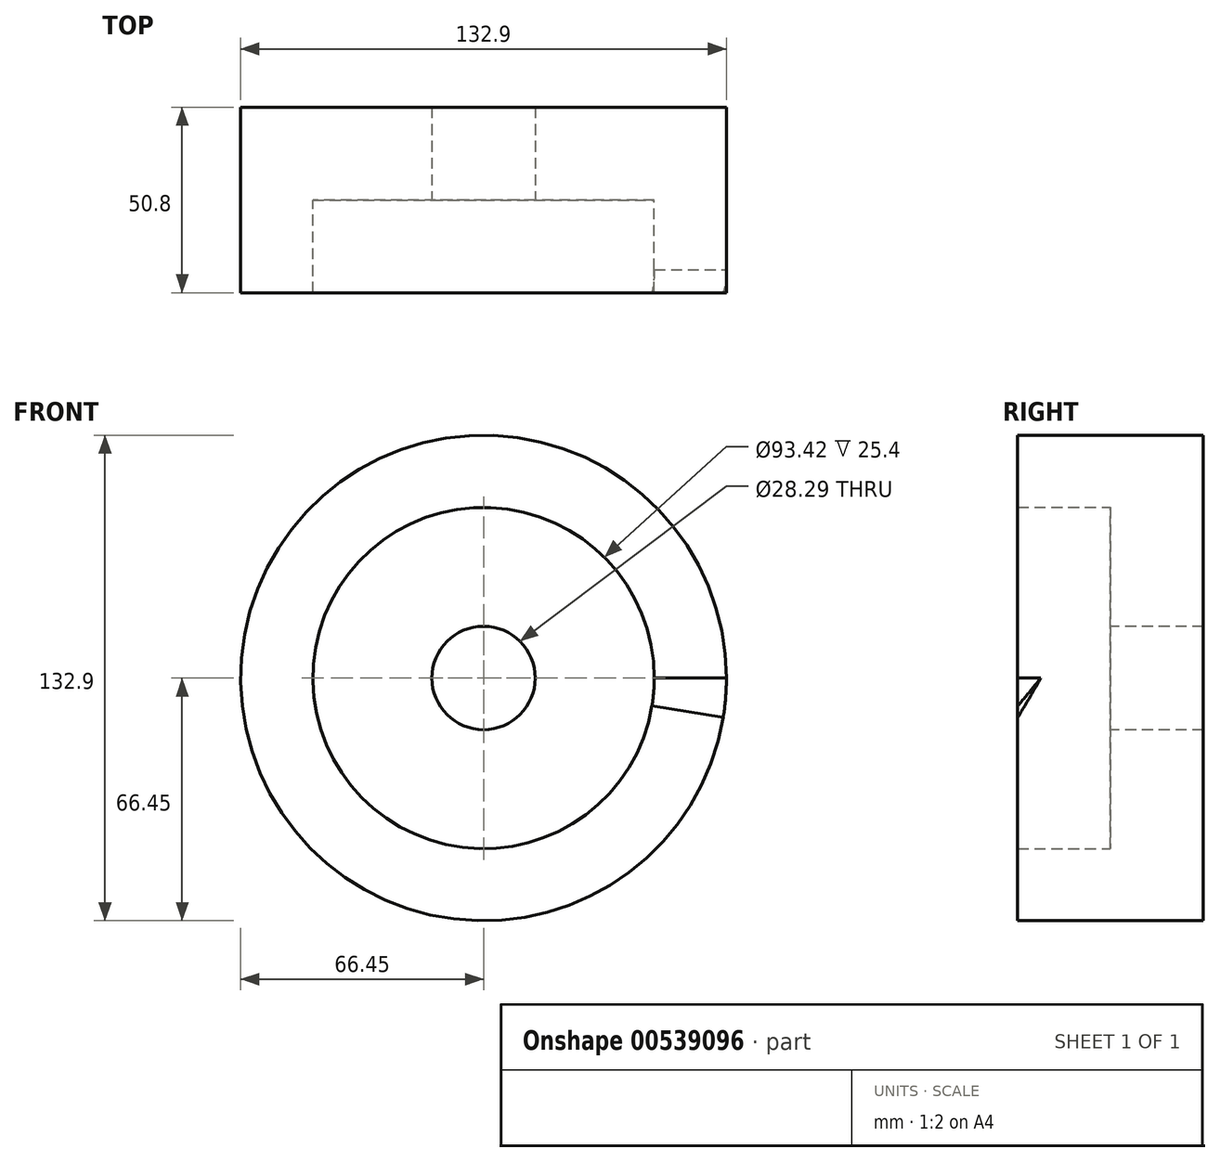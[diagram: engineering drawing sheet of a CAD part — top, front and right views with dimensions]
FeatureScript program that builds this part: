
annotation { "Feature Type Name" : "Feature", "Feature Type Description" : "" }
export const myFeature = defineFeature(function(context is Context, id is Id, definition is map)
    precondition{}
    {
        {
            var Q0;
            Q0=qCreatedBy(makeId("Front.planeOp"),FACE);
            var sketch = newSketch(context, id + "F0", { "sketchPlane" : qUnion([Q0])});
            skCircle(sketch, "E0", {"center": v(0, 0) * mm, "radius": 66.45 * mm});
            skSolve(sketch);
        }
        {
            var Q0;
            Q0 = qSketchRegion(id + "F0", true);
            extrude(context, id + "F1", {"entities" : qUnion([Q0]), "depth" : 25.4 * mm, "offsetDistance" : 25.4 * mm});
        }
        {
            var Q0;
            Q0=makeQuery(id+"F1.opExtrude","CAP_FACE",FACE,{"disambiguationData":[OSD([sQuery(id+"F0.wireOp",EDGE,"E0")])],"isStart":false});
            var sketch = newSketch(context, id + "F2", { "sketchPlane" : qUnion([Q0])});
            skCircle(sketch, "E1", {"center": v(0, 0) * mm, "radius": 46.7 * mm});
            skSolve(sketch);
        }
        {
            var Q0;
            Q0=makeQuery(id+"F2.imprint","IMPRINT",FACE,{"disambiguationData":[TD([[makeQuery(id+"F2.imprint","IMPRINT",EDGE,{"derivedFrom":sQuery(id+"F2.wireOp",EDGE,"E1")}),-1.0]])]});
            extrude(context, id + "F3", {"entities" : qUnion([Q0]), "operationType" : NewBodyOperationType.ADD, "depth" : 25.4 * mm, "offsetDistance" : 25.4 * mm});
        }
        {
            var Q0;
            Q0=makeQuery(id+"F2.imprint","IMPRINT",FACE,{"disambiguationData":[TD([[makeQuery(id+"F2.imprint","IMPRINT",EDGE,{"derivedFrom":sQuery(id+"F2.wireOp",EDGE,"E1")}),1.0]])]});
            var sketch = newSketch(context, id + "F4", { "sketchPlane" : qUnion([Q0])});
            skCircle(sketch, "E2", {"center": v(0, 0) * mm, "radius": 14.15 * mm});
            skSolve(sketch);
        }
        {
            var Q0;
            Q0 = qSketchRegion(id + "F4", true);
            extrude(context, id + "F5", {"entities" : qUnion([Q0]), "operationType" : NewBodyOperationType.REMOVE, "endBound" : BoundingType.THROUGH_ALL, "oppositeDirection" : true, "depth" : 25.4 * mm, "offsetDistance" : 25.4 * mm});
        }
        {
            var Q0;
            Q0=qCreatedBy(makeId("Right.planeOp"),FACE);
            var sketch = newSketch(context, id + "F6", { "sketchPlane" : qUnion([Q0])});
            skLineSegment(sketch, "E3", {"start": v(-44.45, 0) * mm, "end": v(-50.8, 0) * mm});
            skLineSegment(sketch, "E4", {"start": v(-50.8, 0) * mm, "end": v(-50.8, -0.11) * mm});
            skLineSegment(sketch, "E5", {"start": v(-50.8, -0.11) * mm, "end": v(-44.45, 0) * mm});
            skSolve(sketch);
        }
        {
            var Q0;
            Q0=qCreatedBy(makeId("Right.planeOp"),FACE);
            cPlane(context, id + "F7", {"entities" : qUnion([Q0]), "cplaneType" : CPlaneType.OFFSET, "offset" : 66.67 * mm, "width" : 152.4 * mm, "height" : 152.4 * mm});
        }
        {
            var Q0;
            Q0=qCreatedBy(id+"F7.planeOp",FACE);
            var sketch = newSketch(context, id + "F8", { "sketchPlane" : qUnion([Q0])});
            skLineSegment(sketch, "E6", {"start": v(-44.45, 0) * mm, "end": v(-50.8, 0) * mm});
            skLineSegment(sketch, "E7", {"start": v(-50.8, 0) * mm, "end": v(-50.8, -11) * mm});
            skLineSegment(sketch, "E8", {"start": v(-50.8, -11) * mm, "end": v(-44.45, 0) * mm});
            skSolve(sketch);
        }
        {
            var Q1;
            Q1 = qSketchRegion(id + "F6", true);
            var Q2;
            Q2 = qSketchRegion(id + "F8", true);
            loft(context, id + "F9", {"operationType" : NewBodyOperationType.REMOVE, "sheetProfilesArray" : [{ "sheetProfileEntities" : qUnion([Q1]) }, { "sheetProfileEntities" : qUnion([Q2]) }]});
        }
    });
